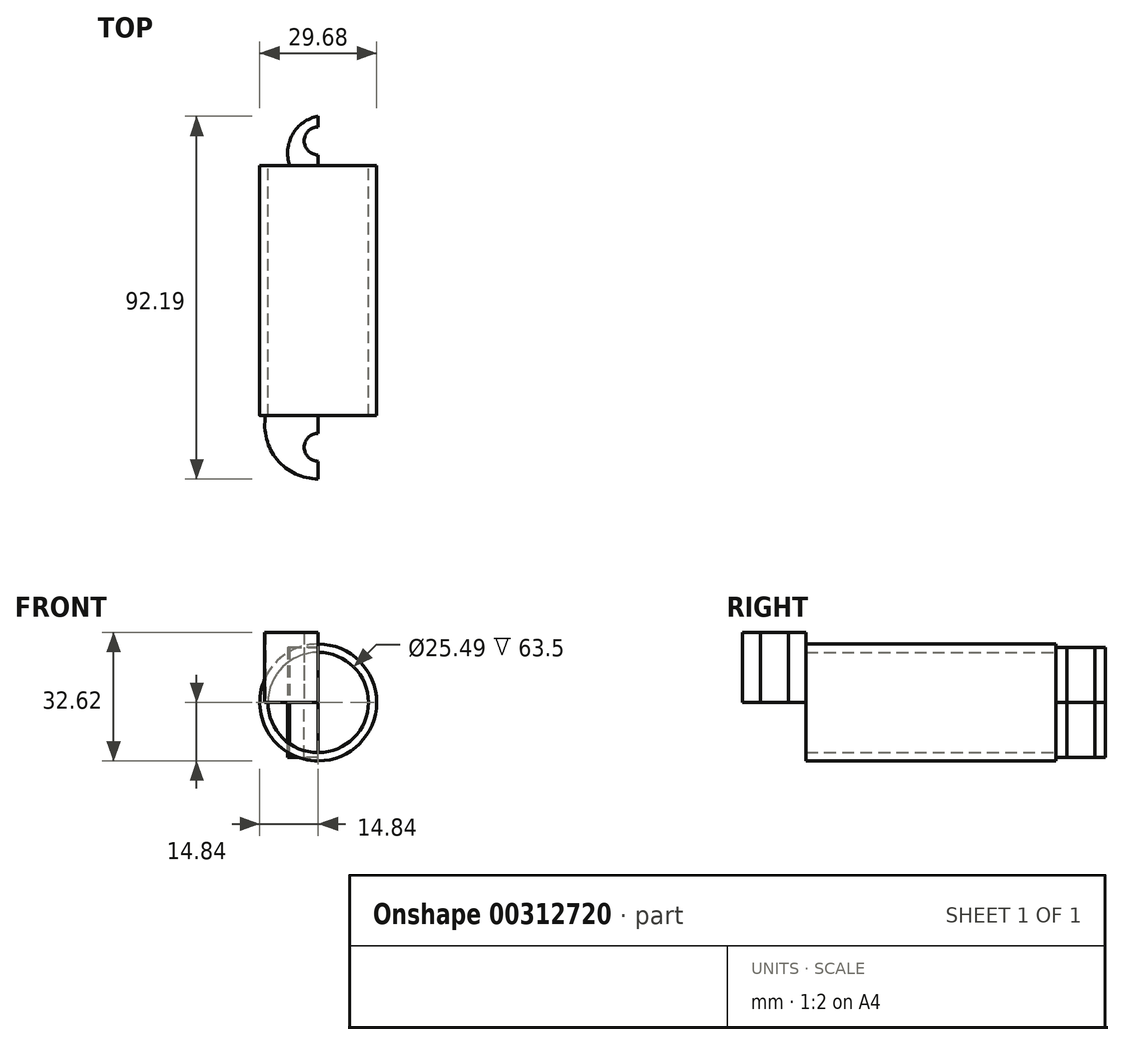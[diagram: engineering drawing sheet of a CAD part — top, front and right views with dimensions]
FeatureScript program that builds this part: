
annotation { "Feature Type Name" : "Feature", "Feature Type Description" : "" }
export const myFeature = defineFeature(function(context is Context, id is Id, definition is map)
    precondition{}
    {
        {
            var Q0;
            Q0=qCreatedBy(makeId("Front.planeOp"),FACE);
            var sketch = newSketch(context, id + "F0", { "sketchPlane" : qUnion([Q0])});
            skCircle(sketch, "E0", {"center": v(0, 0) * mm, "radius": 14.84 * mm});
            skCircle(sketch, "E1", {"center": v(0, 0) * mm, "radius": 12.75 * mm});
            skSolve(sketch);
        }
        {
            var Q0;
            Q0=makeQuery(id+"F0.imprint","IMPRINT",FACE,{"disambiguationData":[TD([[makeQuery(id+"F0.imprint","IMPRINT",EDGE,{"derivedFrom":sQuery(id+"F0.wireOp",EDGE,"E0")}),1.0]])]});
            extrude(context, id + "F1", {"entities" : qUnion([Q0]), "depth" : 63.5 * mm});
        }
        {
            var Q0;
            Q0=qCreatedBy(makeId("Top.planeOp"),FACE);
            var sketch = newSketch(context, id + "F2", { "sketchPlane" : qUnion([Q0])});
            skArc(sketch, "E2", {"start": v(0, 12.59) * mm, "mid": v(-6.5, 7.96) * mm, "end": v(-7.22, 0) * mm});
            skLineSegment(sketch, "E3", {"start": v(0, 0) * mm, "end": v(0, 12.59) * mm});
            skArc(sketch, "E4.MirrorCS", {"start": v(0, 12.59) * mm, "mid": v(6.5, 7.96) * mm, "end": v(7.22, 0) * mm});
            skCircle(sketch, "E5", {"center": v(0, 6.3) * mm, "radius": 3.56 * mm});
            skLineSegment(sketch, "E6", {"start": v(-7.22, 0) * mm, "end": v(7.22, 0) * mm});
            skLineSegment(sketch, "E7", {"start": v(0, 0) * mm, "end": v(0, -63.5) * mm});
            skArc(sketch, "E8", {"start": v(-13.35, -63.5) * mm, "mid": v(-10.44, -74.67) * mm, "end": v(0, -79.6) * mm});
            skLineSegment(sketch, "E9", {"start": v(0, -79.6) * mm, "end": v(0, -63.5) * mm});
            skArc(sketch, "E10.MirrorCS", {"start": v(13.35, -63.5) * mm, "mid": v(10.44, -74.67) * mm, "end": v(0, -79.6) * mm});
            skCircle(sketch, "E11", {"center": v(0, -71.55) * mm, "radius": 3.56 * mm});
            skLineSegment(sketch, "E12", {"start": v(-13.35, -63.5) * mm, "end": v(13.35, -63.5) * mm});
            skSolve(sketch);
        }
        {
            var Q0;
            {var subQ1=sQuery(id+"F2.wireOp",EDGE,"E2");Q0=makeQuery(id+"F2.imprint","IMPRINT",FACE,{"disambiguationData":[TD([[makeQuery(id+"F2.imprint","IMPRINT",EDGE,{"derivedFrom":subQ1}),1.0]])]});}
            var Q1;
            {var subQ0=sQuery(id+"F2.wireOp",EDGE,"E4.MirrorCS");Q1=makeQuery(id+"F2.imprint","IMPRINT",FACE,{"disambiguationData":[TD([[makeQuery(id+"F2.imprint","IMPRINT",EDGE,{"derivedFrom":subQ0}),-1.0]])]});}
            extrude(context, id + "F3", {"entities" : qUnion([Q0, Q1]), "depth" : 13.97 * mm});
        }
        {
            var Q0;
            Q0=makeQuery(id+"F3.opExtrude","CAP_FACE",FACE,{"disambiguationData":[OSD([sQuery(id+"F2.wireOp",EDGE,"E2"),sQuery(id+"F2.wireOp",EDGE,"E4.MirrorCS"),sQuery(id+"F2.wireOp",EDGE,"E5"),sQuery(id+"F2.wireOp",EDGE,"E6")])],"isStart":true});
            extrude(context, id + "F4", {"entities" : qUnion([Q0]), "depth" : 13.97 * mm});
        }
        {
            var Q0;
            {var subQ0=sQuery(id+"F2.wireOp",EDGE,"E10.MirrorCS");Q0=makeQuery(id+"F2.imprint","IMPRINT",FACE,{"disambiguationData":[TD([[makeQuery(id+"F2.imprint","IMPRINT",EDGE,{"derivedFrom":subQ0}),-1.0]])]});}
            var Q1;
            {var subQ5=sQuery(id+"F2.wireOp",EDGE,"E8");Q1=makeQuery(id+"F2.imprint","IMPRINT",FACE,{"disambiguationData":[TD([[makeQuery(id+"F2.imprint","IMPRINT",EDGE,{"derivedFrom":subQ5}),1.0]])]});}
            extrude(context, id + "F5", {"entities" : qUnion([Q0, Q1]), "depth" : 17.78 * mm});
        }
    });
